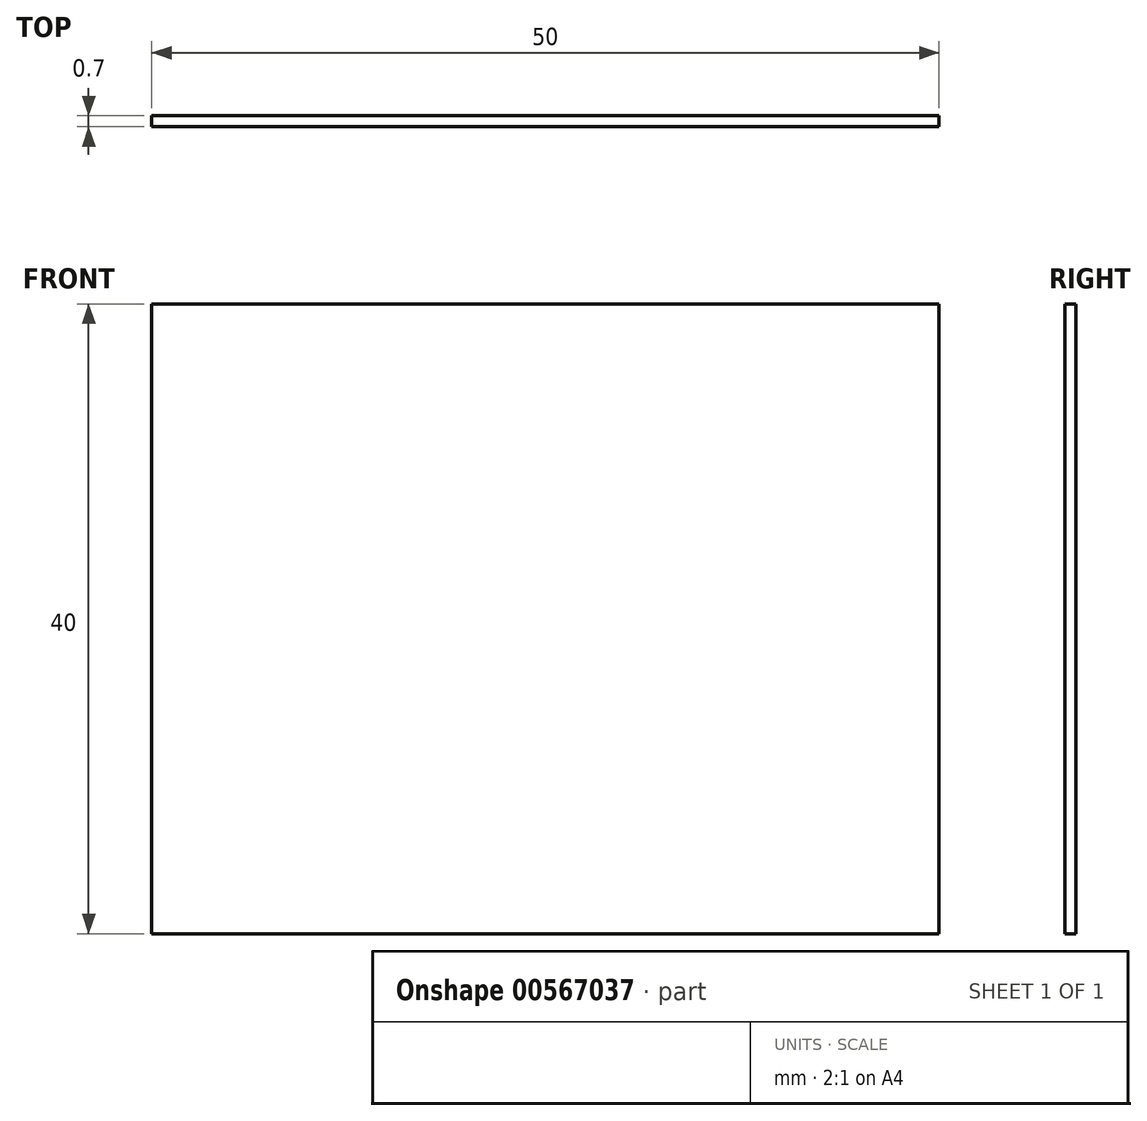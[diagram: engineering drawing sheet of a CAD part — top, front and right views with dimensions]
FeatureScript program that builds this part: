
annotation { "Feature Type Name" : "Feature", "Feature Type Description" : "" }
export const myFeature = defineFeature(function(context is Context, id is Id, definition is map)
    precondition{}
    {
        {
            var Q0;
            Q0=qCreatedBy(makeId("Front.planeOp"),FACE);
            var sketch = newSketch(context, id + "F0", { "sketchPlane" : qUnion([Q0])});
            skLineSegment(sketch, "E0.bottom", {"start": v(-72.69, 73.5) * mm, "end": v(-22.69, 73.5) * mm});
            skLineSegment(sketch, "E0.top", {"start": v(-72.69, 33.5) * mm, "end": v(-22.69, 33.5) * mm});
            skLineSegment(sketch, "E0.left", {"start": v(-72.69, 73.5) * mm, "end": v(-72.69, 33.5) * mm});
            skLineSegment(sketch, "E0.right", {"start": v(-22.69, 73.5) * mm, "end": v(-22.69, 33.5) * mm});
            skSolve(sketch);
        }
        {
            var Q0;
            Q0 = qSketchRegion(id + "F0", true);
            extrude(context, id + "F1", {"entities" : qUnion([Q0]), "depth" : 0.7 * mm, "offsetDistance" : 25 * mm});
        }
    });
